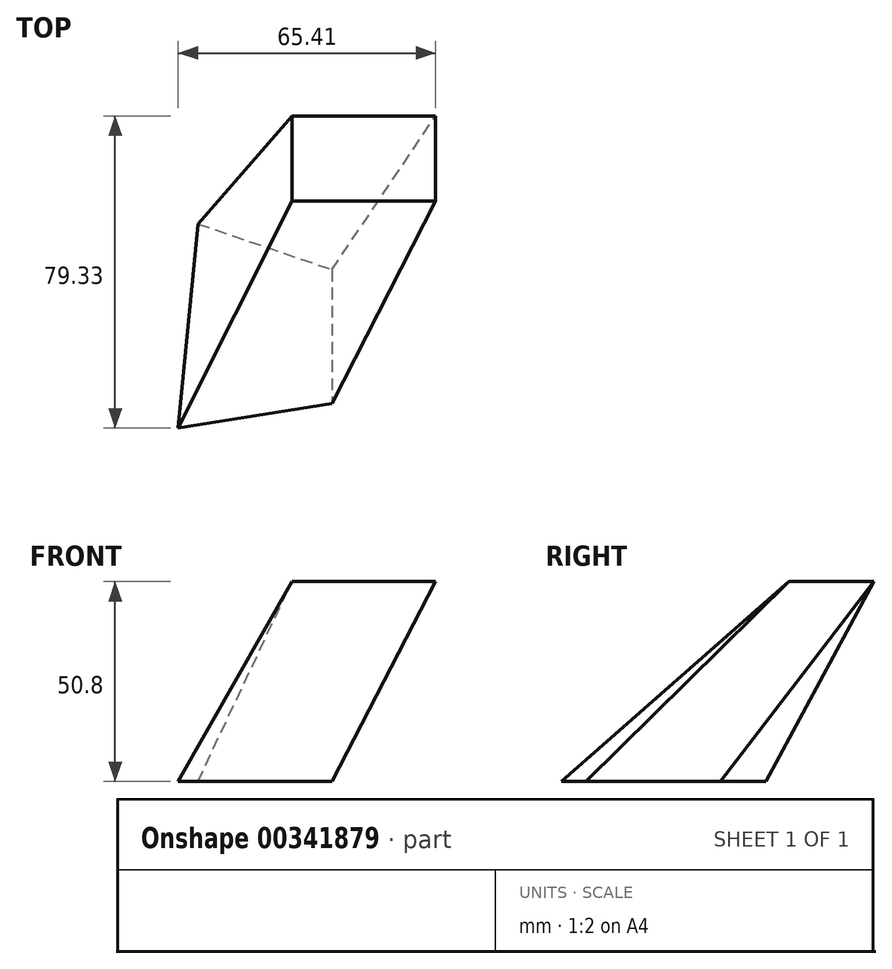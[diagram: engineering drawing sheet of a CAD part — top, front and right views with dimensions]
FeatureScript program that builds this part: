
annotation { "Feature Type Name" : "Feature", "Feature Type Description" : "" }
export const myFeature = defineFeature(function(context is Context, id is Id, definition is map)
    precondition{}
    {
        {
            var Q0;
            Q0=qCreatedBy(makeId("Top.planeOp"),FACE);
            var sketch = newSketch(context, id + "F0", { "sketchPlane" : qUnion([Q0])});
            skCircle(sketch, "E0", {"center": v(-62.28, 52.52) * mm, "radius": 11.18 * mm});
            skLineSegment(sketch, "E1.bottom", {"start": v(23.25, 37.16) * mm, "end": v(59.79, 37.16) * mm});
            skLineSegment(sketch, "E1.top", {"start": v(23.25, 15.57) * mm, "end": v(59.79, 15.57) * mm});
            skLineSegment(sketch, "E1.left", {"start": v(23.25, 37.16) * mm, "end": v(23.25, 15.57) * mm});
            skLineSegment(sketch, "E1.right", {"start": v(59.79, 37.16) * mm, "end": v(59.79, 15.57) * mm});
            skLineSegment(sketch, "E2", {"start": v(-55, -17.45) * mm, "end": v(-20.95, -29.08) * mm});
            skLineSegment(sketch, "E3", {"start": v(-20.95, -29.08) * mm, "end": v(-20.95, -63.13) * mm});
            skLineSegment(sketch, "E4", {"start": v(-20.95, -63.13) * mm, "end": v(-59.98, -69.35) * mm});
            skLineSegment(sketch, "E5", {"start": v(-59.98, -69.35) * mm, "end": v(-55, -17.45) * mm});
            skLineSegment(sketch, "E6", {"start": v(-82.91, 71.7) * mm, "end": v(-82.91, 30.26) * mm, "construction": true});
            skSolve(sketch);
        }
        {
            var Q0;
            Q0=qCreatedBy(makeId("Top.planeOp"),FACE);
            cPlane(context, id + "F1", {"entities" : qUnion([Q0]), "cplaneType" : CPlaneType.OFFSET, "offset" : 50.8 * mm, "width" : 152.4 * mm, "height" : 152.4 * mm});
        }
        {
            var Q0;
            Q0=qCreatedBy(id+"F1.planeOp",FACE);
            var sketch = newSketch(context, id + "F2", { "sketchPlane" : qUnion([Q0])});
            skCircle(sketch, "E7.0", {"center": v(-116.64, 25.35) * mm, "radius": 11.18 * mm});
            skLineSegment(sketch, "E7.1.0", {"start": v(-31.1, 9.98) * mm, "end": v(-31.1, -11.6) * mm});
            skLineSegment(sketch, "E7.1.1", {"start": v(-31.1, -11.6) * mm, "end": v(5.43, -11.6) * mm});
            skLineSegment(sketch, "E7.1.2", {"start": v(5.43, -11.6) * mm, "end": v(5.43, 9.98) * mm});
            skLineSegment(sketch, "E7.1.3", {"start": v(5.43, 9.98) * mm, "end": v(-31.1, 9.98) * mm});
            skLineSegment(sketch, "E7.2.0", {"start": v(-109.36, -44.63) * mm, "end": v(-114.34, -96.53) * mm});
            skLineSegment(sketch, "E7.2.1", {"start": v(-114.34, -96.53) * mm, "end": v(-75.3, -90.3) * mm});
            skLineSegment(sketch, "E7.2.2", {"start": v(-75.3, -90.3) * mm, "end": v(-75.3, -56.26) * mm});
            skLineSegment(sketch, "E7.2.3", {"start": v(-75.3, -56.26) * mm, "end": v(-109.36, -44.63) * mm});
            skSolve(sketch);
        }
        {
            var Q0;
            Q0=makeQuery(id+"F0.imprint","IMPRINT",FACE,{"disambiguationData":[TD([[makeQuery(id+"F0.imprint","IMPRINT",EDGE,{"derivedFrom":sQuery(id+"F0.wireOp",EDGE,"E2")}),-1.0]])]});
            var Q1;
            Q1=makeQuery(id+"F2.imprint","IMPRINT",FACE,{"disambiguationData":[TD([[makeQuery(id+"F2.imprint","IMPRINT",EDGE,{"derivedFrom":sQuery(id+"F2.wireOp",EDGE,"E7.1.0")}),1.0]])]});
            loft(context, id + "F3", {"sheetProfilesArray" : [{ "sheetProfileEntities" : qUnion([Q0]) }, { "sheetProfileEntities" : qUnion([Q1]) }]});
        }
    });
